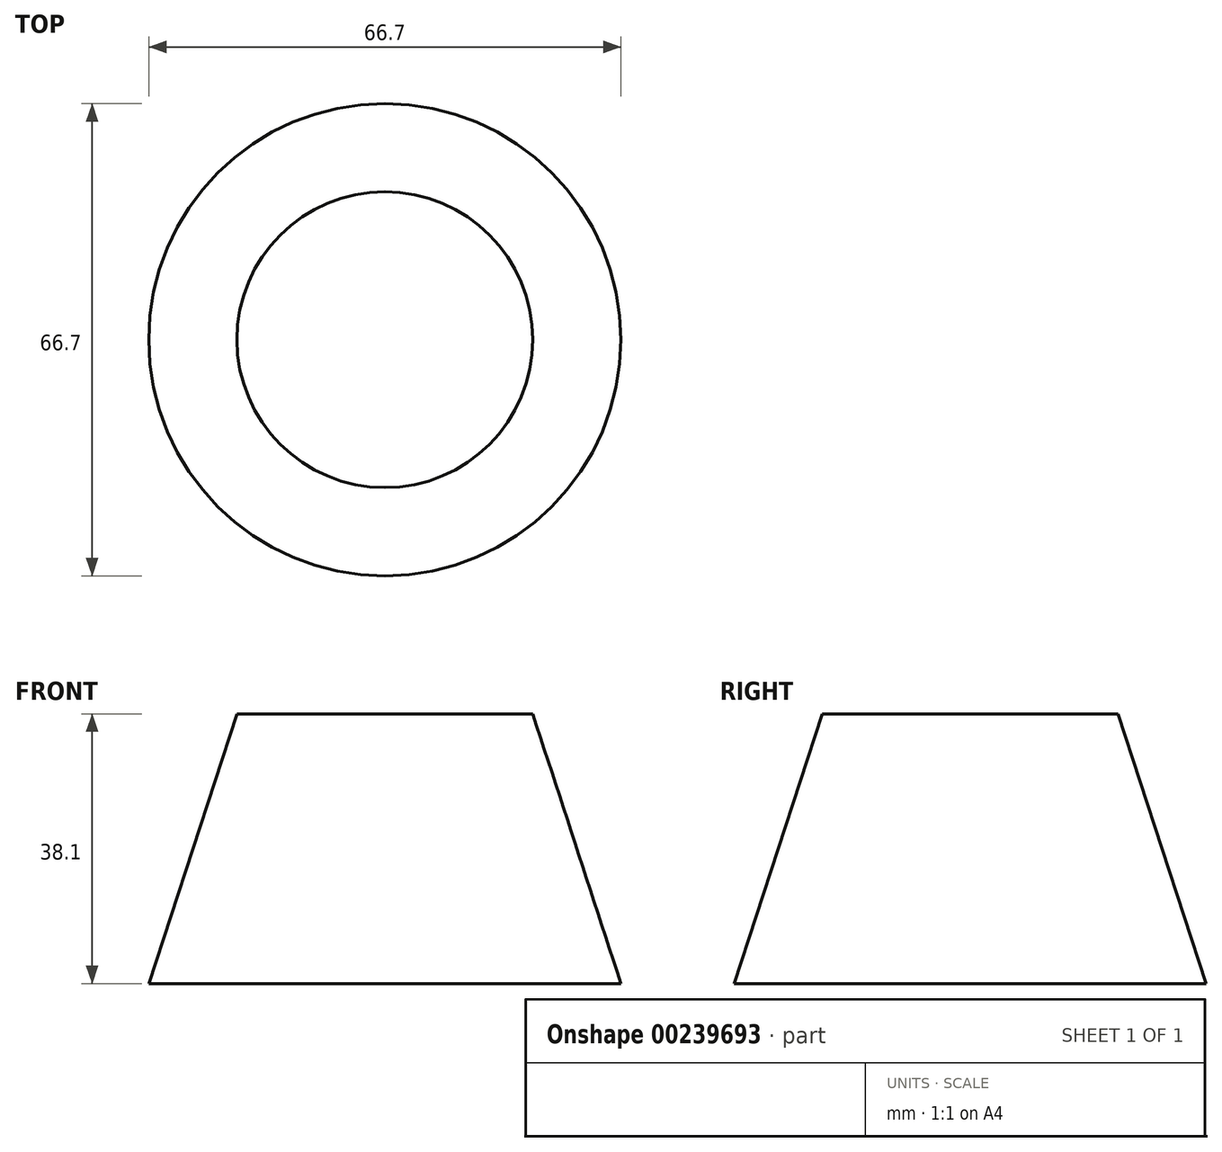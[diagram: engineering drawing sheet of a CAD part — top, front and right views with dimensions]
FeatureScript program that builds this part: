
annotation { "Feature Type Name" : "Feature", "Feature Type Description" : "" }
export const myFeature = defineFeature(function(context is Context, id is Id, definition is map)
    precondition{}
    {
        {
            var Q0;
            Q0=qCreatedBy(makeId("Top.planeOp"),FACE);
            var sketch = newSketch(context, id + "F0", { "sketchPlane" : qUnion([Q0])});
            skCircle(sketch, "E0", {"center": v(0, 0) * mm, "radius": 38.32 * mm});
            skCircle(sketch, "E1", {"center": v(0, 0) * mm, "radius": 33.35 * mm});
            skLineSegment(sketch, "E2", {"start": v(-4.46, 38.06) * mm, "end": v(-4.46, 33.05) * mm});
            skLineSegment(sketch, "E3", {"start": v(3.59, 38.15) * mm, "end": v(3.59, 33.16) * mm});
            skLineSegment(sketch, "E4", {"start": v(3.63, -33.15) * mm, "end": v(3.63, -38.15) * mm});
            skLineSegment(sketch, "E5", {"start": v(-5.46, -37.93) * mm, "end": v(-5.46, -32.9) * mm});
            skSolve(sketch);
        }
        {
            var Q0;
            Q0=qCreatedBy(makeId("Top.planeOp"),FACE);
            cPlane(context, id + "F1", {"entities" : qUnion([Q0]), "cplaneType" : CPlaneType.OFFSET, "offset" : 38.1 * mm, "width" : 152.4 * mm, "height" : 152.4 * mm});
        }
        {
            var Q0;
            Q0=qCreatedBy(id+"F1.planeOp",FACE);
            var sketch = newSketch(context, id + "F2", { "sketchPlane" : qUnion([Q0])});
            skCircle(sketch, "E6", {"center": v(0, 0) * mm, "radius": 20.9 * mm});
            skSolve(sketch);
        }
        {
            var Q0;
            {var subQ0=sQuery(id+"F0.wireOp",EDGE,"E1");var subQ1=makeQuery(id+"F0.imprint","INTERSECT",VERTEX,{"derivedFrom":[subQ0,sQuery(id+"F0.wireOp",EDGE,"E2")]});Q0=makeQuery(id+"F0.imprint","IMPRINT",FACE,{"disambiguationData":[TD([[makeQuery(id+"F0.imprint","IMPRINT",EDGE,{"disambiguationData":[TD([[subQ1,1.0]])],"derivedFrom":subQ0}),1.0]])]});}
            var Q1;
            Q1=makeQuery(id+"F2.imprint","IMPRINT",FACE,{"disambiguationData":[TD([[makeQuery(id+"F2.imprint","IMPRINT",EDGE,{"derivedFrom":sQuery(id+"F2.wireOp",EDGE,"E6")}),1.0]])]});
            loft(context, id + "F3", {"sheetProfilesArray" : [{ "sheetProfileEntities" : qUnion([Q0]) }, { "sheetProfileEntities" : qUnion([Q1]) }]});
        }
    });
